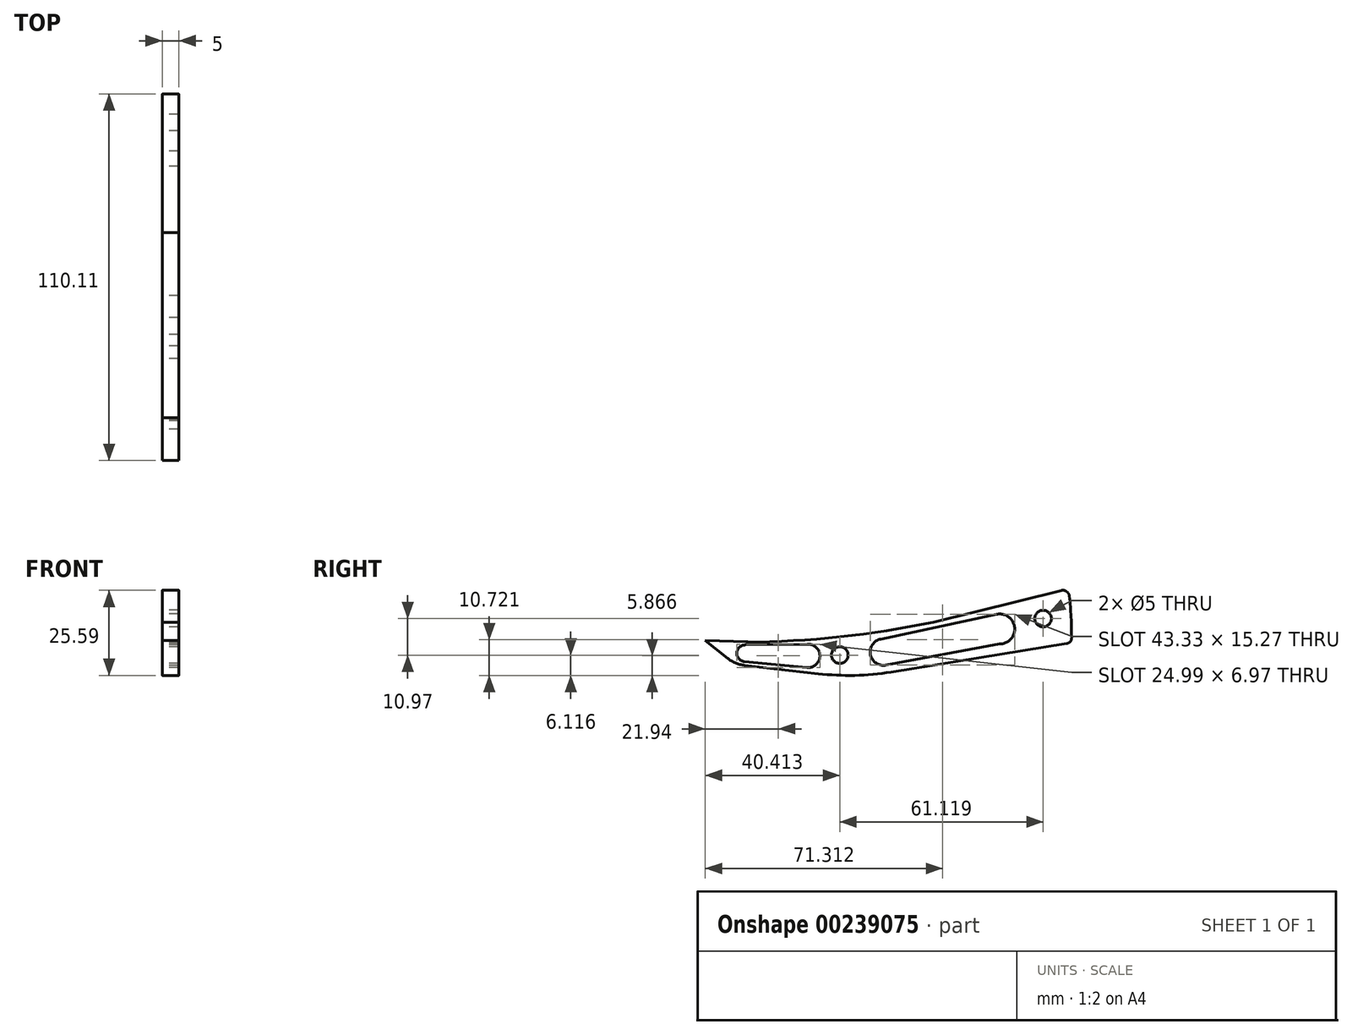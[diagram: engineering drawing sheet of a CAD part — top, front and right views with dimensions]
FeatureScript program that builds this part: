
annotation { "Feature Type Name" : "Feature", "Feature Type Description" : "" }
export const myFeature = defineFeature(function(context is Context, id is Id, definition is map)
    precondition{}
    {
        {
            var Q0;
            Q0=qCreatedBy(makeId("Right.planeOp"),FACE);
            var sketch = newSketch(context, id + "F0", { "sketchPlane" : qUnion([Q0])});
            skArc(sketch, "E0", {"start": v(21.96, 10.72) * mm, "mid": v(21.96, 10.73) * mm, "end": v(21.96, 10.73) * mm});
            skArc(sketch, "E1", {"start": v(120, 12) * mm, "mid": v(119.84, 18.28) * mm, "end": v(119.34, 24.54) * mm});
            skArc(sketch, "E2", {"start": v(21.96, 10.72) * mm, "mid": v(22.32, 10.75) * mm, "end": v(22.67, 10.8) * mm});
            skLineSegment(sketch, "E3", {"start": v(78.34, 16.72) * mm, "end": v(116.87, 26.27) * mm});
            skPoint(sketch, "E4.third.point", {"position": v(50.09, 12.3) * mm});
            skPoint(sketch, "E4.third.point.positionSnap0", {"position": v(50.09, 13.72) * mm});
            skArc(sketch, "E5", {"start": v(22.18, 10.73) * mm, "mid": v(50.41, 12.34) * mm, "end": v(78.34, 16.72) * mm});
            skCircle(sketch, "E6", {"center": v(111.42, 17.83) * mm, "radius": 2.5 * mm});
            skCircle(sketch, "E7", {"center": v(50.3, 6.86) * mm, "radius": 2.5 * mm});
            skLineSegment(sketch, "E8", {"start": v(9.89, 11.27) * mm, "end": v(16.5, 5.93) * mm});
            skLineSegment(sketch, "E9", {"start": v(21.65, 3.78) * mm, "end": v(43.83, 1.25) * mm});
            skLineSegment(sketch, "E10", {"start": v(65.72, 1.77) * mm, "end": v(118.6, 10.35) * mm});
            skArc(sketch, "E11.filletArc", {"start": v(16.5, 5.93) * mm, "mid": v(18.92, 4.5) * mm, "end": v(21.65, 3.78) * mm});
            skPoint(sketch, "E12.visualSharp", {"position": v(54.8, 0) * mm});
            skArc(sketch, "E12.filletArc", {"start": v(43.83, 1.25) * mm, "mid": v(54.8, 0.76) * mm, "end": v(65.72, 1.77) * mm});
            skLineSegment(sketch, "E13", {"start": v(9.89, 11.27) * mm, "end": v(22.67, 10.8) * mm});
            skPoint(sketch, "E14.visualSharp", {"position": v(120, 10.58) * mm});
            skArc(sketch, "E14.filletArc", {"start": v(118.6, 10.35) * mm, "mid": v(119.6, 10.92) * mm, "end": v(120, 12) * mm});
            skPoint(sketch, "E15.visualSharp", {"position": v(119.08, 26.82) * mm});
            skArc(sketch, "E15.filletArc", {"start": v(119.34, 24.54) * mm, "mid": v(118.5, 25.97) * mm, "end": v(116.87, 26.27) * mm});
            skArc(sketch, "E16", {"start": v(98.33, 10.19) * mm, "mid": v(102.87, 15.15) * mm, "end": v(97.42, 19.08) * mm});
            skArc(sketch, "E17", {"start": v(40.5, 3.12) * mm, "mid": v(44.32, 6.58) * mm, "end": v(40.54, 10.1) * mm});
            skArc(sketch, "E18", {"start": v(21.86, 9.9) * mm, "mid": v(19.33, 7.53) * mm, "end": v(21.61, 4.92) * mm});
            skLineSegment(sketch, "E19", {"start": v(21.75, 9.9) * mm, "end": v(41.04, 10.1) * mm});
            skLineSegment(sketch, "E20", {"start": v(21.58, 4.92) * mm, "end": v(40.5, 3.12) * mm});
            skArc(sketch, "E21", {"start": v(62.63, 11.67) * mm, "mid": v(59.54, 6.98) * mm, "end": v(64.2, 3.83) * mm});
            skLineSegment(sketch, "E22", {"start": v(97.42, 19.08) * mm, "end": v(62.63, 11.67) * mm});
            skLineSegment(sketch, "E23", {"start": v(98.33, 10.19) * mm, "end": v(64.2, 3.83) * mm});
            skSolve(sketch);
        }
        {
            var Q0;
            {var subQ9=sQuery(id+"F0.wireOp",EDGE,"Z2RfFS8F-fJbA-lgiH-K7Vn-SxlDWFhEWRw2");Q0=makeQuery(id+"F0.imprint","IMPRINT",FACE,{"disambiguationData":[TD([[makeQuery(id+"F0.imprint","IMPRINT",EDGE,{"derivedFrom":subQ9}),-1.0]])]});}
            var Q1;
            Q1=qSketchRegion(id+"F0",true);
            extrude(context, id + "F1", {"entities" : qUnion([Q0, Q1]), "depth" : 5 * mm});
        }
    });
